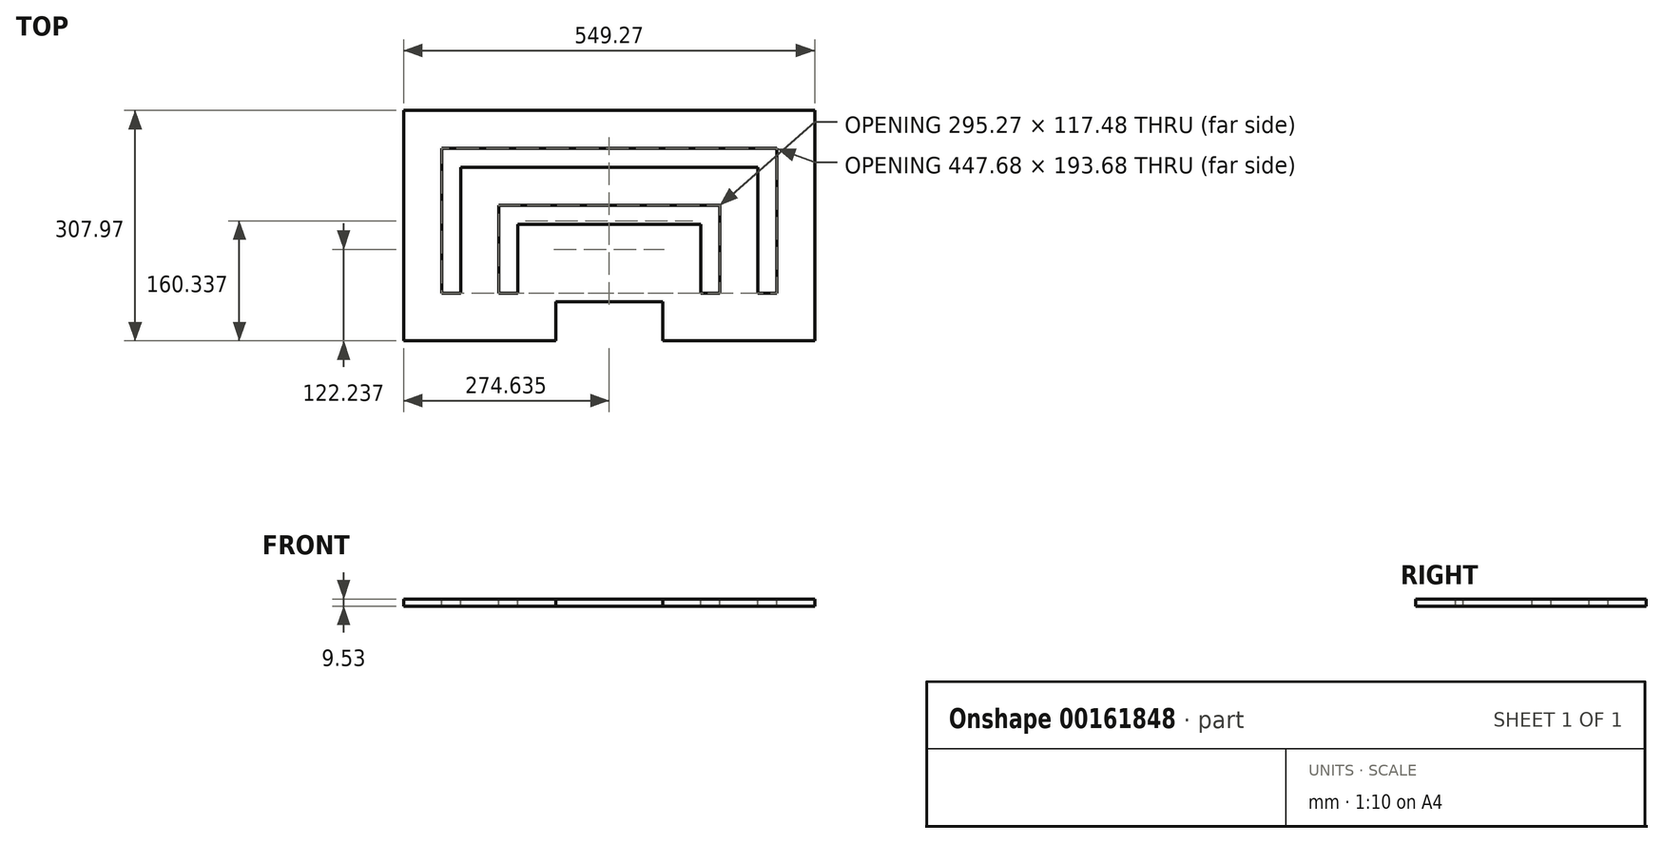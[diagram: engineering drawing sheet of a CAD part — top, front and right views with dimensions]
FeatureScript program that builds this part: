
annotation { "Feature Type Name" : "Feature", "Feature Type Description" : "" }
export const myFeature = defineFeature(function(context is Context, id is Id, definition is map)
    precondition{}
    {
        {
            var Q0;
            Q0=qCreatedBy(makeId("Top.planeOp"),FACE);
            var sketch = newSketch(context, id + "F0", { "sketchPlane" : qUnion([Q0])});
            skLineSegment(sketch, "E0", {"start": v(-258.02, 177.35) * mm, "end": v(291.25, 177.35) * mm});
            skLineSegment(sketch, "E1", {"start": v(-258.02, 177.35) * mm, "end": v(-258.02, -130.62) * mm});
            skLineSegment(sketch, "E2", {"start": v(291.25, 177.35) * mm, "end": v(291.25, -130.62) * mm});
            skLineSegment(sketch, "E3", {"start": v(-258.02, -130.62) * mm, "end": v(-54.82, -130.62) * mm});
            skLineSegment(sketch, "E4", {"start": v(291.25, -130.62) * mm, "end": v(88.05, -130.62) * mm});
            skLineSegment(sketch, "E5", {"start": v(-54.82, -130.62) * mm, "end": v(-54.82, -78.23) * mm});
            skLineSegment(sketch, "E6", {"start": v(88.05, -130.62) * mm, "end": v(88.05, -78.23) * mm});
            skLineSegment(sketch, "E7", {"start": v(-54.82, -78.23) * mm, "end": v(88.05, -78.23) * mm});
            skSolve(sketch);
        }
        {
            var Q0;
            Q0 = qSketchRegion(id + "F0", true);
            extrude(context, id + "F1", {"entities" : qUnion([Q0]), "depth" : 9.52 * mm});
        }
        {
            var Q0;
            Q0=makeQuery(id+"F1.opExtrude","CAP_FACE",FACE,{"disambiguationData":[OSD([sQuery(id+"F0.wireOp",EDGE,"E0"),sQuery(id+"F0.wireOp",EDGE,"E1"),sQuery(id+"F0.wireOp",EDGE,"E2"),sQuery(id+"F0.wireOp",EDGE,"E3"),sQuery(id+"F0.wireOp",EDGE,"E4"),sQuery(id+"F0.wireOp",EDGE,"E5"),sQuery(id+"F0.wireOp",EDGE,"E6"),sQuery(id+"F0.wireOp",EDGE,"E7")])],"isStart":false});
            var sketch = newSketch(context, id + "F2", { "sketchPlane" : qUnion([Q0])});
            skLineSegment(sketch, "E8", {"start": v(-207.22, -67.12) * mm, "end": v(-207.22, 126.55) * mm});
            skLineSegment(sketch, "E9", {"start": v(240.45, 126.55) * mm, "end": v(240.45, -67.12) * mm});
            skLineSegment(sketch, "E10", {"start": v(-207.22, 126.55) * mm, "end": v(240.45, 126.55) * mm});
            skLineSegment(sketch, "E11", {"start": v(-207.22, -67.12) * mm, "end": v(-181.82, -67.12) * mm});
            skLineSegment(sketch, "E12", {"start": v(240.45, -67.12) * mm, "end": v(215.05, -67.12) * mm});
            skLineSegment(sketch, "E13", {"start": v(-181.82, -67.12) * mm, "end": v(-181.82, 101.15) * mm});
            skLineSegment(sketch, "E14", {"start": v(-181.82, 101.15) * mm, "end": v(215.05, 101.15) * mm});
            skLineSegment(sketch, "E15", {"start": v(215.05, 101.15) * mm, "end": v(215.05, -67.12) * mm});
            skLineSegment(sketch, "E16", {"start": v(-131.02, -67.12) * mm, "end": v(-105.62, -67.12) * mm});
            skLineSegment(sketch, "E17", {"start": v(-131.02, -67.12) * mm, "end": v(-131.02, 50.35) * mm});
            skLineSegment(sketch, "E18", {"start": v(164.25, -67.12) * mm, "end": v(138.85, -67.12) * mm});
            skLineSegment(sketch, "E19", {"start": v(164.25, -67.12) * mm, "end": v(164.25, 50.35) * mm});
            skLineSegment(sketch, "E20", {"start": v(164.25, 50.35) * mm, "end": v(-131.02, 50.35) * mm});
            skLineSegment(sketch, "E21", {"start": v(-105.62, -67.12) * mm, "end": v(-105.62, 24.95) * mm});
            skLineSegment(sketch, "E22", {"start": v(-105.62, 24.95) * mm, "end": v(138.85, 24.95) * mm});
            skLineSegment(sketch, "E23", {"start": v(138.85, 24.95) * mm, "end": v(138.85, -67.12) * mm});
            skSolve(sketch);
        }
        {
            var Q0;
            Q0 = qSketchRegion(id + "F2", true);
            extrude(context, id + "F3", {"entities" : qUnion([Q0]), "operationType" : NewBodyOperationType.REMOVE, "endBound" : BoundingType.THROUGH_ALL, "oppositeDirection" : true, "depth" : 25.4 * mm});
        }
    });
